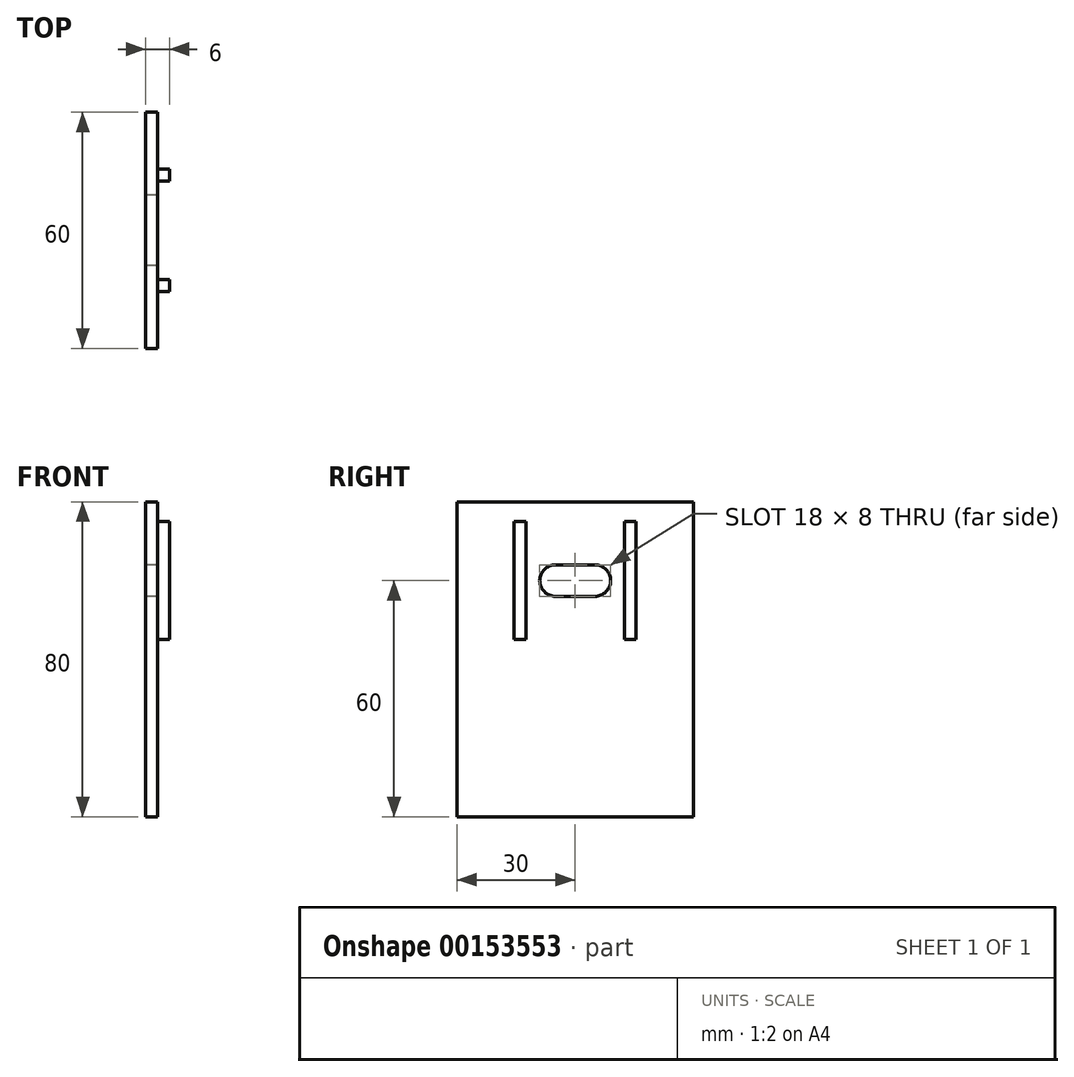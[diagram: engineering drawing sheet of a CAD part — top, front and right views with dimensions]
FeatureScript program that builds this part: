
annotation { "Feature Type Name" : "Feature", "Feature Type Description" : "" }
export const myFeature = defineFeature(function(context is Context, id is Id, definition is map)
    precondition{}
    {
        {
            var Q0;
            Q0=qCreatedBy(makeId("Right.planeOp"),FACE);
            var sketch = newSketch(context, id + "F0", { "sketchPlane" : qUnion([Q0])});
            skLineSegment(sketch, "E0.bottom", {"start": v(0, 0) * mm, "end": v(-60, 0) * mm});
            skLineSegment(sketch, "E0.top", {"start": v(0, 80) * mm, "end": v(-60, 80) * mm});
            skLineSegment(sketch, "E0.left", {"start": v(0, 0) * mm, "end": v(0, 80) * mm});
            skLineSegment(sketch, "E0.right", {"start": v(-60, 0) * mm, "end": v(-60, 80) * mm});
            skArc(sketch, "E1", {"start": v(-35, 64) * mm, "mid": v(-39, 60) * mm, "end": v(-35, 56) * mm});
            skArc(sketch, "E2", {"start": v(-25, 56) * mm, "mid": v(-21, 60) * mm, "end": v(-25, 64) * mm});
            skLineSegment(sketch, "E3", {"start": v(-35, 60) * mm, "end": v(-25, 60) * mm, "construction": true});
            skLineSegment(sketch, "E4", {"start": v(-35, 64) * mm, "end": v(-25, 64) * mm});
            skLineSegment(sketch, "E5", {"start": v(-35, 56) * mm, "end": v(-25, 56) * mm});
            skSolve(sketch);
        }
        {
            var Q0;
            Q0=makeQuery(id+"F0.imprint","IMPRINT",FACE,{"disambiguationData":[TD([[makeQuery(id+"F0.imprint","IMPRINT",EDGE,{"derivedFrom":sQuery(id+"F0.wireOp",EDGE,"E0.bottom")}),-1.0]])]});
            extrude(context, id + "F1", {"entities" : qUnion([Q0]), "depth" : 3 * mm});
        }
        {
            var Q0;
            Q0=makeQuery(id+"F1.opExtrude","CAP_FACE",FACE,{"disambiguationData":[OSD([sQuery(id+"F0.wireOp",EDGE,"E0.bottom"),sQuery(id+"F0.wireOp",EDGE,"E0.top"),sQuery(id+"F0.wireOp",EDGE,"E0.left"),sQuery(id+"F0.wireOp",EDGE,"E0.right"),sQuery(id+"F0.wireOp",EDGE,"E1"),sQuery(id+"F0.wireOp",EDGE,"E2"),sQuery(id+"F0.wireOp",EDGE,"E4"),sQuery(id+"F0.wireOp",EDGE,"E5")])],"isStart":false});
            var sketch = newSketch(context, id + "F2", { "sketchPlane" : qUnion([Q0])});
            skArc(sketch, "E6.0", {"start": v(-35, 64) * mm, "mid": v(-39, 60) * mm, "end": v(-35, 56) * mm, "construction": true});
            skLineSegment(sketch, "E7.0", {"start": v(-35, 64) * mm, "end": v(-25, 64) * mm, "construction": true});
            skArc(sketch, "E8.0", {"start": v(-25, 56) * mm, "mid": v(-21, 60) * mm, "end": v(-25, 64) * mm, "construction": true});
            skLineSegment(sketch, "E9.0", {"start": v(-35, 56) * mm, "end": v(-25, 56) * mm, "construction": true});
            skPoint(sketch, "E10.startSnap0", {"position": v(-39, 60) * mm});
            skLineSegment(sketch, "E11", {"start": v(-35, 60) * mm, "end": v(-25, 60) * mm, "construction": true});
            skCircle(sketch, "E12", {"center": v(-30, 60) * mm, "radius": 12.5 * mm, "construction": true});
            skLineSegment(sketch, "E13.bottom", {"start": v(-42.5, 45) * mm, "end": v(-45.5, 45) * mm});
            skLineSegment(sketch, "E13.top", {"start": v(-42.5, 75) * mm, "end": v(-45.5, 75) * mm});
            skLineSegment(sketch, "E13.left", {"start": v(-42.5, 45) * mm, "end": v(-42.5, 75) * mm});
            skLineSegment(sketch, "E13.right", {"start": v(-45.5, 45) * mm, "end": v(-45.5, 75) * mm});
            skLineSegment(sketch, "E14.bottom", {"start": v(-14.5, 45) * mm, "end": v(-17.5, 45) * mm});
            skLineSegment(sketch, "E14.top", {"start": v(-14.5, 75) * mm, "end": v(-17.5, 75) * mm});
            skLineSegment(sketch, "E14.left", {"start": v(-14.5, 45) * mm, "end": v(-14.5, 75) * mm});
            skLineSegment(sketch, "E14.right", {"start": v(-17.5, 45) * mm, "end": v(-17.5, 75) * mm});
            skSolve(sketch);
        }
        {
            var Q0;
            Q0 = qSketchRegion(id + "F2", true);
            extrude(context, id + "F3", {"entities" : qUnion([Q0]), "operationType" : NewBodyOperationType.ADD, "depth" : 3 * mm});
        }
    });
